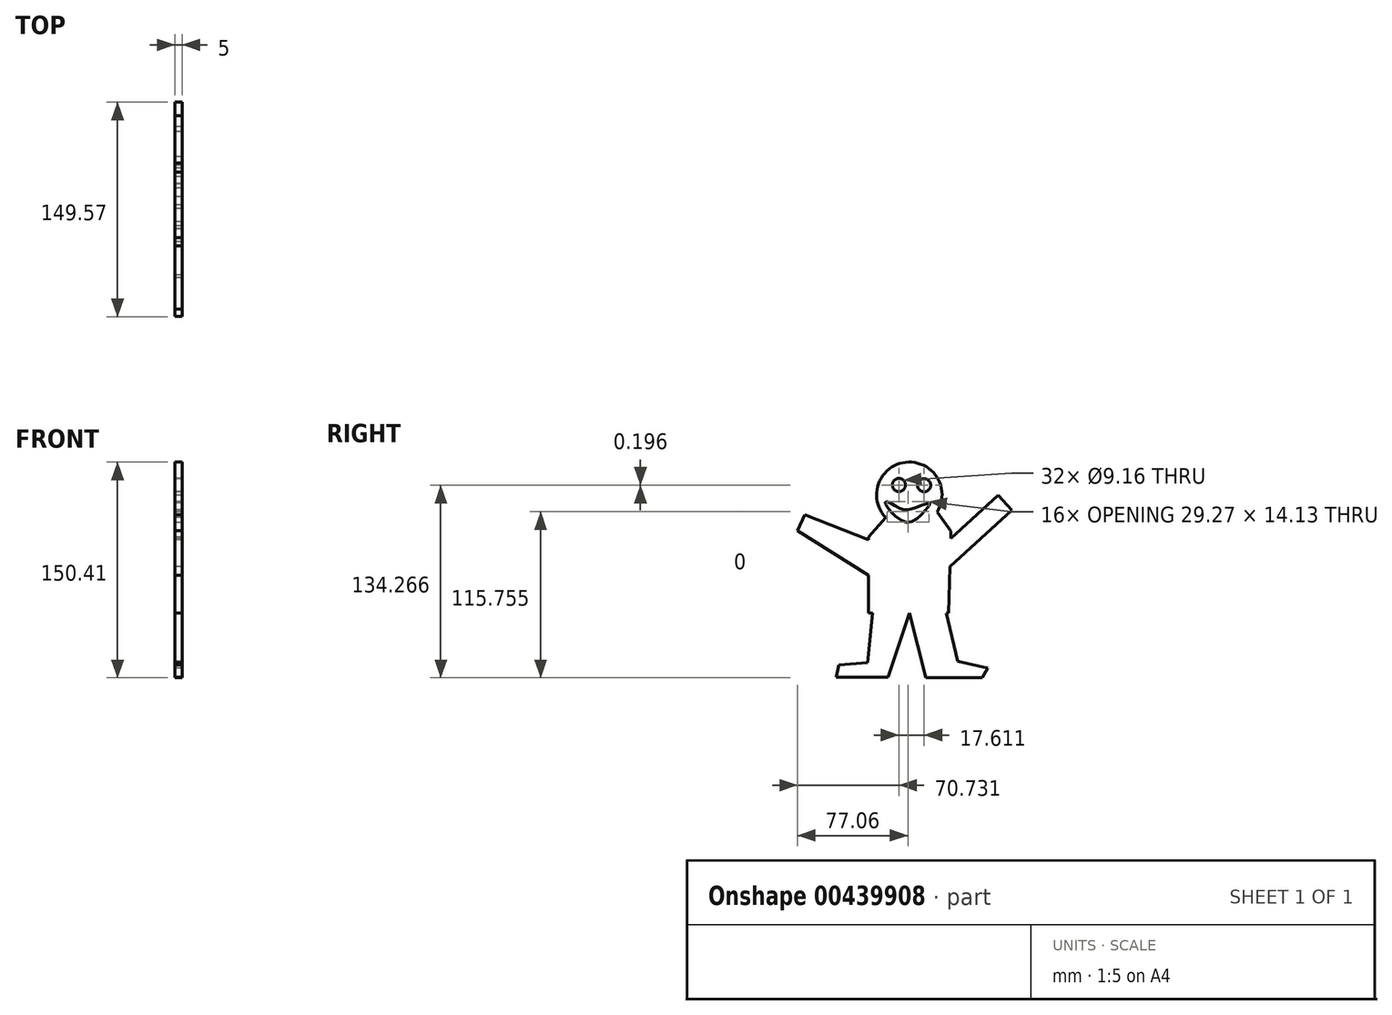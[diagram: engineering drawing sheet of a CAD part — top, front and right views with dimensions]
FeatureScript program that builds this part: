
annotation { "Feature Type Name" : "Feature", "Feature Type Description" : "" }
export const myFeature = defineFeature(function(context is Context, id is Id, definition is map)
    precondition{}
    {
        {
            var Q0;
            Q0=qCreatedBy(makeId("Right.planeOp"),FACE);
            var sketch = newSketch(context, id + "F0", { "sketchPlane" : qUnion([Q0])});
            skCircle(sketch, "E0", {"center": v(-6.07, 55.95) * mm, "radius": 22.85 * mm});
            skLineSegment(sketch, "E1", {"start": v(-22.6, 40.17) * mm, "end": v(-34.67, 26.39) * mm});
            skLineSegment(sketch, "E2", {"start": v(-34.67, 26.39) * mm, "end": v(-34.67, -26.39) * mm});
            skLineSegment(sketch, "E3", {"start": v(-34.67, -26.39) * mm, "end": v(21.4, -26.39) * mm});
            skLineSegment(sketch, "E4", {"start": v(21.4, -26.39) * mm, "end": v(22.94, 30.5) * mm});
            skLineSegment(sketch, "E5", {"start": v(22.94, 30.5) * mm, "end": v(13.43, 44.05) * mm});
            skLineSegment(sketch, "E6", {"start": v(-34.67, 24.57) * mm, "end": v(-78.97, 42.03) * mm});
            skLineSegment(sketch, "E7", {"start": v(-78.97, 42.03) * mm, "end": v(-84.07, 30.86) * mm});
            skLineSegment(sketch, "E8", {"start": v(-84.07, 30.86) * mm, "end": v(-34.67, 0) * mm});
            skLineSegment(sketch, "E9", {"start": v(22.8, 25.43) * mm, "end": v(56.02, 55.72) * mm});
            skLineSegment(sketch, "E10", {"start": v(56.02, 55.72) * mm, "end": v(65.5, 45.32) * mm});
            skLineSegment(sketch, "E11", {"start": v(65.5, 45.32) * mm, "end": v(22.27, 5.9) * mm});
            skLineSegment(sketch, "E12", {"start": v(-31.7, -26.39) * mm, "end": v(-35.27, -61.04) * mm});
            skLineSegment(sketch, "E13", {"start": v(-35.27, -61.04) * mm, "end": v(-55.07, -62.8) * mm});
            skLineSegment(sketch, "E14", {"start": v(-55.07, -62.8) * mm, "end": v(-57.03, -71.43) * mm});
            skLineSegment(sketch, "E15", {"start": v(-57.03, -71.43) * mm, "end": v(-20.77, -71.43) * mm});
            skLineSegment(sketch, "E16", {"start": v(-20.77, -71.43) * mm, "end": v(-6.06, -26.39) * mm});
            skLineSegment(sketch, "E17", {"start": v(-6.06, -26.39) * mm, "end": v(5.49, -71.62) * mm});
            skLineSegment(sketch, "E18", {"start": v(5.49, -71.62) * mm, "end": v(44.88, -71.62) * mm});
            skLineSegment(sketch, "E19", {"start": v(44.88, -71.62) * mm, "end": v(48.6, -64.96) * mm});
            skLineSegment(sketch, "E20", {"start": v(48.6, -64.96) * mm, "end": v(27.63, -60.26) * mm});
            skLineSegment(sketch, "E21", {"start": v(27.63, -60.26) * mm, "end": v(19.73, -26.39) * mm});
            skCircle(sketch, "E22", {"center": v(-13.34, 62.84) * mm, "radius": 4.58 * mm});
            skCircle(sketch, "E23", {"center": v(4.27, 62.65) * mm, "radius": 4.58 * mm});
            skFitSpline(sketch, "E24", {"points": [v(-12.6, 46.54) * mm, v(-3.13, 46.54) * mm, v(8.19, 50.12) * mm, v(4.73, 44.73) * mm, v(-9.82, 37.2) * mm, v(-22.73, 51.1) * mm, v(-12.6, 46.54) * mm]});
            skSolve(sketch);
        }
        {
            var Q0;
            {var subQ0=sQuery(id+"F0.wireOp",EDGE,"E6");Q0=makeQuery(id+"F0.imprint","IMPRINT",FACE,{"disambiguationData":[TD([[makeQuery(id+"F0.imprint","IMPRINT",EDGE,{"derivedFrom":subQ0}),1.0]])]});}
            var Q1;
            {var subQ10=sQuery(id+"F0.wireOp",EDGE,"E1");Q1=makeQuery(id+"F0.imprint","IMPRINT",FACE,{"disambiguationData":[TD([[makeQuery(id+"F0.imprint","IMPRINT",EDGE,{"derivedFrom":subQ10}),1.0]])]});}
            var Q2;
            {var subQ0=sQuery(id+"F0.wireOp",EDGE,"E9");Q2=makeQuery(id+"F0.imprint","IMPRINT",FACE,{"disambiguationData":[TD([[makeQuery(id+"F0.imprint","IMPRINT",EDGE,{"derivedFrom":subQ0}),-1.0]])]});}
            var Q3;
            {var subQ0=sQuery(id+"F0.wireOp",EDGE,"E17");Q3=makeQuery(id+"F0.imprint","IMPRINT",FACE,{"disambiguationData":[TD([[makeQuery(id+"F0.imprint","IMPRINT",EDGE,{"derivedFrom":subQ0}),1.0]])]});}
            var Q4;
            {var subQ0=sQuery(id+"F0.wireOp",EDGE,"E12");Q4=makeQuery(id+"F0.imprint","IMPRINT",FACE,{"disambiguationData":[TD([[makeQuery(id+"F0.imprint","IMPRINT",EDGE,{"derivedFrom":subQ0}),1.0]])]});}
            var Q5;
            Q5=makeQuery(id+"F0.imprint","IMPRINT",FACE,{"disambiguationData":[TD([[makeQuery(id+"F0.imprint","IMPRINT",EDGE,{"derivedFrom":sQuery(id+"F0.wireOp",EDGE,"E22")}),-1.0]])]});
            extrude(context, id + "F1", {"entities" : qUnion([Q0, Q1, Q2, Q3, Q4, Q5]), "depth" : 5 * mm});
        }
    });
